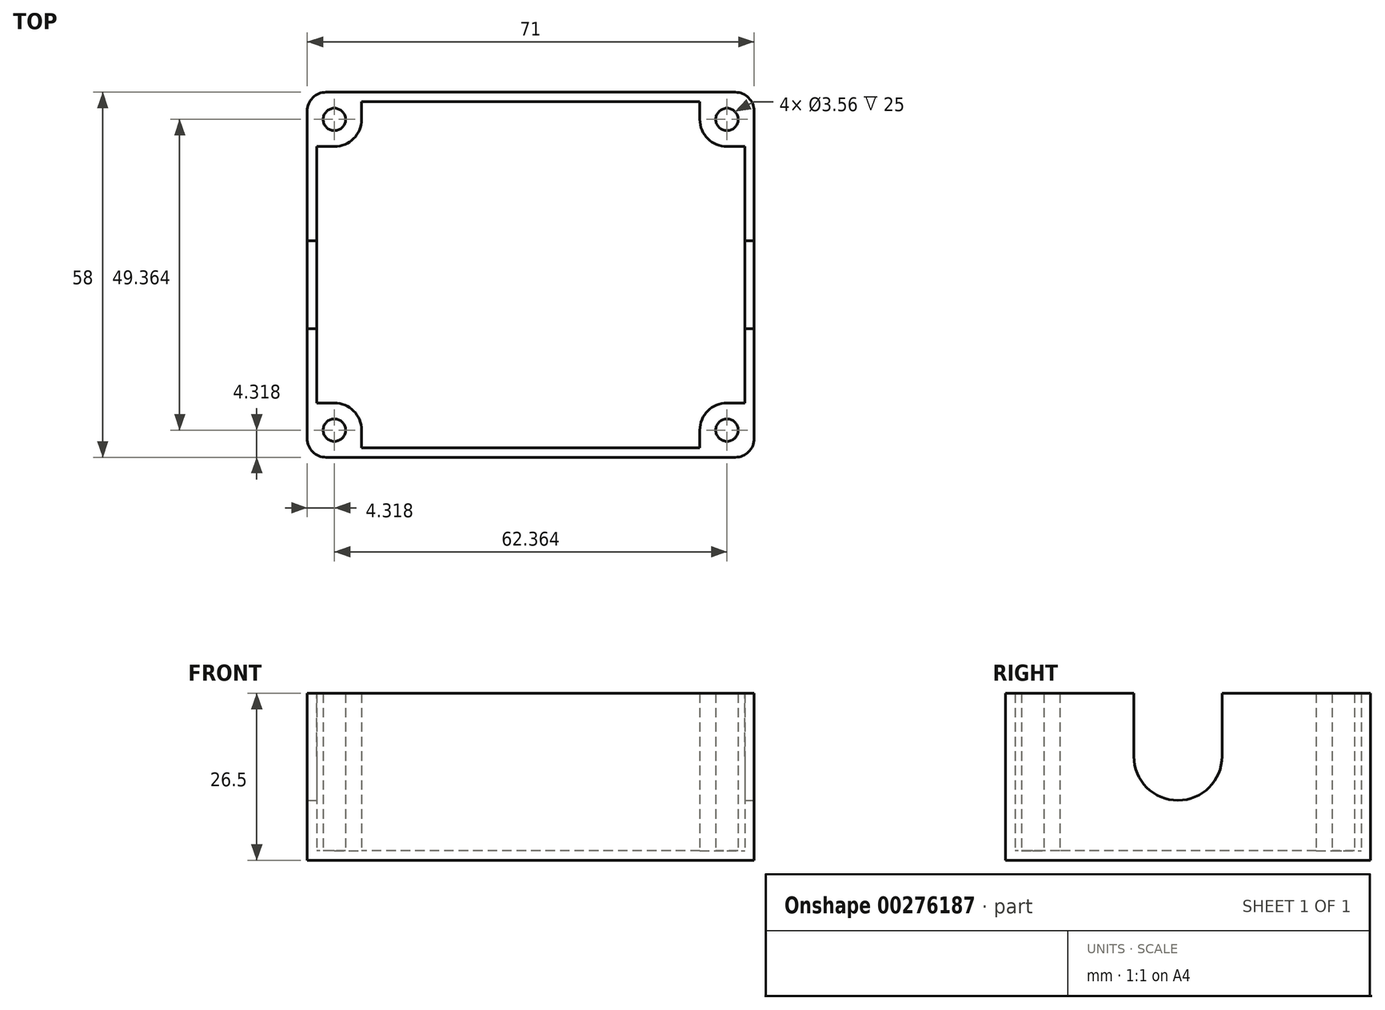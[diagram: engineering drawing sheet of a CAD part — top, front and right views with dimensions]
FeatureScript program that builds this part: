
annotation { "Feature Type Name" : "Feature", "Feature Type Description" : "" }
export const myFeature = defineFeature(function(context is Context, id is Id, definition is map)
    precondition{}
    {
        {
            var Q0;
            Q0=qCreatedBy(makeId("Top.planeOp"),FACE);
            var sketch = newSketch(context, id + "F0", { "sketchPlane" : qUnion([Q0])});
            skLineSegment(sketch, "E0.bottom", {"start": v(35.5, 29) * mm, "end": v(-35.5, 29) * mm});
            skLineSegment(sketch, "E0.top", {"start": v(35.5, -29) * mm, "end": v(-35.5, -29) * mm});
            skLineSegment(sketch, "E0.left", {"start": v(35.5, 29) * mm, "end": v(35.5, -29) * mm});
            skLineSegment(sketch, "E0.right", {"start": v(-35.5, 29) * mm, "end": v(-35.5, -29) * mm});
            skPoint(sketch, "E0.middle", {"position": v(0, 0) * mm});
            skSolve(sketch);
        }
        {
            var Q0;
            Q0=qSketchRegion(id+"F0",true);
            extrude(context, id + "F1", {"entities" : qUnion([Q0]), "depth" : 1.5 * mm});
        }
        {
            var Q0;
            Q0=makeQuery(id+"F1.opExtrude","CAP_FACE",FACE,{"disambiguationData":[OSD([sQuery(id+"F0.wireOp",EDGE,"E0.bottom"),sQuery(id+"F0.wireOp",EDGE,"E0.top"),sQuery(id+"F0.wireOp",EDGE,"E0.left"),sQuery(id+"F0.wireOp",EDGE,"E0.right")])],"isStart":false});
            var sketch = newSketch(context, id + "F2", { "sketchPlane" : qUnion([Q0])});
            skLineSegment(sketch, "E1.bottom", {"start": v(27.94, 15.24) * mm, "end": v(-27.94, 15.24) * mm, "construction": true});
            skLineSegment(sketch, "E1.top", {"start": v(27.94, -15.24) * mm, "end": v(-27.94, -15.24) * mm, "construction": true});
            skLineSegment(sketch, "E1.left", {"start": v(27.94, 15.24) * mm, "end": v(27.94, -15.24) * mm, "construction": true});
            skLineSegment(sketch, "E1.right", {"start": v(-27.94, 15.24) * mm, "end": v(-27.94, -15.24) * mm, "construction": true});
            skPoint(sketch, "E1.middle", {"position": v(0, 0) * mm});
            skCircle(sketch, "E2", {"center": v(-27.94, 15.24) * mm, "radius": 1.51 * mm});
            skCircle(sketch, "E3", {"center": v(27.94, 15.24) * mm, "radius": 1.51 * mm});
            skCircle(sketch, "E4", {"center": v(27.94, -15.24) * mm, "radius": 1.51 * mm});
            skCircle(sketch, "E5", {"center": v(-27.94, -15.24) * mm, "radius": 1.51 * mm});
            skLineSegment(sketch, "E6.bottom", {"start": v(31.75, 19.05) * mm, "end": v(-31.75, 19.05) * mm, "construction": true});
            skLineSegment(sketch, "E6.top", {"start": v(31.75, -19.05) * mm, "end": v(-31.75, -19.05) * mm, "construction": true});
            skLineSegment(sketch, "E6.left", {"start": v(31.75, 19.05) * mm, "end": v(31.75, -19.05) * mm, "construction": true});
            skLineSegment(sketch, "E6.right", {"start": v(-31.75, 19.05) * mm, "end": v(-31.75, -19.05) * mm, "construction": true});
            skSolve(sketch);
        }
        {
            var Q0;
            Q0=makeQuery(id+"F1.opExtrude","CAP_FACE",FACE,{"disambiguationData":[OSD([sQuery(id+"F0.wireOp",EDGE,"E0.bottom"),sQuery(id+"F0.wireOp",EDGE,"E0.top"),sQuery(id+"F0.wireOp",EDGE,"E0.left"),sQuery(id+"F0.wireOp",EDGE,"E0.right")])],"isStart":false});
            var sketch = newSketch(context, id + "F3", { "sketchPlane" : qUnion([Q0])});
            skLineSegment(sketch, "E7.0", {"start": v(35.5, 29) * mm, "end": v(-31.93, 29) * mm});
            skLineSegment(sketch, "E8.0", {"start": v(-35.5, 23.99) * mm, "end": v(-35.5, -29) * mm});
            skLineSegment(sketch, "E9.0", {"start": v(35.5, -29) * mm, "end": v(-35.5, -29) * mm});
            skLineSegment(sketch, "E10.0", {"start": v(35.5, 29) * mm, "end": v(35.5, -29) * mm});
            skLineSegment(sketch, "E11.0", {"start": v(26.86, 27.5) * mm, "end": v(-26.86, 27.5) * mm});
            skLineSegment(sketch, "E11.1", {"start": v(34, 20.36) * mm, "end": v(34, -20.36) * mm});
            skLineSegment(sketch, "E11.2", {"start": v(26.86, -27.5) * mm, "end": v(-26.86, -27.5) * mm});
            skLineSegment(sketch, "E11.3", {"start": v(-34, 20.36) * mm, "end": v(-34, -20.36) * mm});
            skPoint(sketch, "E12.visualSharp", {"position": v(-35.5, 29) * mm});
            skLineSegment(sketch, "E13", {"start": v(-35.5, 23.99) * mm, "end": v(-35.5, 29) * mm});
            skLineSegment(sketch, "E14", {"start": v(-31.93, 29) * mm, "end": v(-35.5, 29) * mm});
            skPoint(sketch, "E15.middle", {"position": v(0, 0) * mm});
            skLineSegment(sketch, "E16", {"start": v(-35.5, -25.9) * mm, "end": v(-35.5, -25.9) * mm});
            skArc(sketch, "E17", {"start": v(-26.86, -24.68) * mm, "mid": v(-28.13, -21.63) * mm, "end": v(-31.18, -20.36) * mm});
            skCircle(sketch, "E18", {"center": v(-31.18, -24.68) * mm, "radius": 1.78 * mm});
            skLineSegment(sketch, "E19", {"start": v(-31.18, -20.36) * mm, "end": v(-34, -20.36) * mm});
            skLineSegment(sketch, "E20", {"start": v(-26.86, -24.68) * mm, "end": v(-26.86, -27.5) * mm});
            skLineSegment(sketch, "E21.MirrorCS", {"start": v(-26.86, 24.68) * mm, "end": v(-26.86, 27.5) * mm});
            skArc(sketch, "E22.MirrorCS", {"start": v(-26.86, 24.68) * mm, "mid": v(-28.13, 21.63) * mm, "end": v(-31.18, 20.36) * mm});
            skLineSegment(sketch, "E23.MirrorCS", {"start": v(-31.18, 20.36) * mm, "end": v(-34, 20.36) * mm});
            skCircle(sketch, "E24.MirrorC", {"center": v(-31.18, 24.68) * mm, "radius": 1.78 * mm});
            skLineSegment(sketch, "E25.MirrorCS", {"start": v(26.86, -24.68) * mm, "end": v(26.86, -27.5) * mm});
            skArc(sketch, "E26.MirrorCS", {"start": v(26.86, -24.68) * mm, "mid": v(28.13, -21.63) * mm, "end": v(31.18, -20.36) * mm});
            skCircle(sketch, "E27.MirrorC", {"center": v(31.18, -24.68) * mm, "radius": 1.78 * mm});
            skLineSegment(sketch, "E28.MirrorCS", {"start": v(31.18, -20.36) * mm, "end": v(34, -20.36) * mm});
            skLineSegment(sketch, "E29.MirrorCS", {"start": v(31.18, 20.36) * mm, "end": v(34, 20.36) * mm});
            skArc(sketch, "E30.MirrorCS", {"start": v(26.86, 24.68) * mm, "mid": v(28.13, 21.63) * mm, "end": v(31.18, 20.36) * mm});
            skCircle(sketch, "E31.MirrorC", {"center": v(31.18, 24.68) * mm, "radius": 1.78 * mm});
            skLineSegment(sketch, "E32.MirrorCS", {"start": v(26.86, 24.68) * mm, "end": v(26.86, 27.5) * mm});
            skLineSegment(sketch, "E33.bottom", {"start": v(-31.18, 24.68) * mm, "end": v(31.18, 24.68) * mm, "construction": true});
            skLineSegment(sketch, "E33.top", {"start": v(-31.18, -24.68) * mm, "end": v(31.18, -24.68) * mm, "construction": true});
            skLineSegment(sketch, "E33.left", {"start": v(-31.18, 24.68) * mm, "end": v(-31.18, -24.68) * mm, "construction": true});
            skLineSegment(sketch, "E33.right", {"start": v(31.18, 24.68) * mm, "end": v(31.18, -24.68) * mm, "construction": true});
            skSolve(sketch);
        }
        {
            var Q0;
            Q0=makeQuery(id+"F3.imprint","IMPRINT",FACE,{"disambiguationData":[TD([[makeQuery(id+"F3.imprint","IMPRINT",EDGE,{"derivedFrom":sQuery(id+"F3.wireOp",EDGE,"E7.0")}),1.0]])]});
            extrude(context, id + "F4", {"entities" : qUnion([Q0]), "operationType" : NewBodyOperationType.ADD, "depth" : 25 * mm});
        }
        {
            var Q0;
            Q0=makeQuery(id+"F4.boolean.opBoolean","MERGE",FACE,{"derivedFrom":[makeQuery(id+"F1.opExtrude","SWEPT_FACE",FACE,{"disambiguationData":[OSD([sQuery(id+"F0.wireOp",EDGE,"E0.left")])]}),makeQuery(id+"F4.opExtrude","SWEPT_FACE",FACE,{"disambiguationData":[OSD([sQuery(id+"F3.wireOp",EDGE,"E10.0")])]})]});
            var sketch = newSketch(context, id + "F5", { "sketchPlane" : qUnion([Q0])});
            skArc(sketch, "E34", {"start": v(-8.6, 16.5) * mm, "mid": v(-1.6, 9.5) * mm, "end": v(5.4, 16.5) * mm});
            skLineSegment(sketch, "E35", {"start": v(-8.6, 16.5) * mm, "end": v(-8.6, 26.5) * mm});
            skLineSegment(sketch, "E36", {"start": v(5.4, 16.5) * mm, "end": v(5.4, 26.5) * mm});
            skLineSegment(sketch, "E37", {"start": v(5.4, 26.5) * mm, "end": v(-8.6, 26.5) * mm});
            skCircle(sketch, "E38", {"center": v(-1.6, 16.5) * mm, "radius": 6.25 * mm, "construction": true});
            skPoint(sketch, "E39", {"position": v(-1.6, 26.5) * mm});
            skSolve(sketch);
        }
        {
            var Q0;
            Q0=qSketchRegion(id+"F5",true);
            extrude(context, id + "F6", {"entities" : qUnion([Q0]), "operationType" : NewBodyOperationType.REMOVE, "endBound" : BoundingType.THROUGH_ALL, "oppositeDirection" : true, "depth" : 25.4 * mm});
        }
        {
            var Q0;
            Q0=makeQuery(id+"F4.boolean.opBoolean","MERGE",EDGE,{"derivedFrom":[makeQuery(id+"F1.opExtrude","SWEPT_EDGE",EDGE,{"disambiguationData":[OSD([sQuery(id+"F0.wireOp",EDGE,"E0.bottom"),sQuery(id+"F0.wireOp",EDGE,"E0.left")])]}),makeQuery(id+"F4.opExtrude","SWEPT_EDGE",EDGE,{"disambiguationData":[OSD([sQuery(id+"F3.wireOp",EDGE,"E7.0"),sQuery(id+"F3.wireOp",EDGE,"E10.0")])]})]});
            var Q1;
            Q1=makeQuery(id+"F4.boolean.opBoolean","MERGE",EDGE,{"derivedFrom":[makeQuery(id+"F1.opExtrude","SWEPT_EDGE",EDGE,{"disambiguationData":[OSD([sQuery(id+"F0.wireOp",EDGE,"E0.top"),sQuery(id+"F0.wireOp",EDGE,"E0.left")])]}),makeQuery(id+"F4.opExtrude","SWEPT_EDGE",EDGE,{"disambiguationData":[OSD([sQuery(id+"F3.wireOp",EDGE,"E9.0"),sQuery(id+"F3.wireOp",EDGE,"E10.0")])]})]});
            var Q2;
            Q2=makeQuery(id+"F4.boolean.opBoolean","MERGE",EDGE,{"derivedFrom":[makeQuery(id+"F1.opExtrude","SWEPT_EDGE",EDGE,{"disambiguationData":[OSD([sQuery(id+"F0.wireOp",EDGE,"E0.bottom"),sQuery(id+"F0.wireOp",EDGE,"E0.right")])]}),makeQuery(id+"F4.opExtrude","SWEPT_EDGE",EDGE,{"disambiguationData":[OSD([sQuery(id+"F3.wireOp",EDGE,"E13"),sQuery(id+"F3.wireOp",EDGE,"E14")])]})]});
            var Q3;
            Q3=makeQuery(id+"F4.boolean.opBoolean","MERGE",EDGE,{"derivedFrom":[makeQuery(id+"F1.opExtrude","SWEPT_EDGE",EDGE,{"disambiguationData":[OSD([sQuery(id+"F0.wireOp",EDGE,"E0.top"),sQuery(id+"F0.wireOp",EDGE,"E0.right")])]}),makeQuery(id+"F4.opExtrude","SWEPT_EDGE",EDGE,{"disambiguationData":[OSD([sQuery(id+"F3.wireOp",EDGE,"E8.0"),sQuery(id+"F3.wireOp",EDGE,"E9.0")])]})]});
            fillet(context, id + "F7", {"entities" : qUnion([Q0, Q1, Q2, Q3]), "radius" : 3 * mm, "tangentPropagation" : true, "allowEdgeOverflow" : false});
        }
    });
